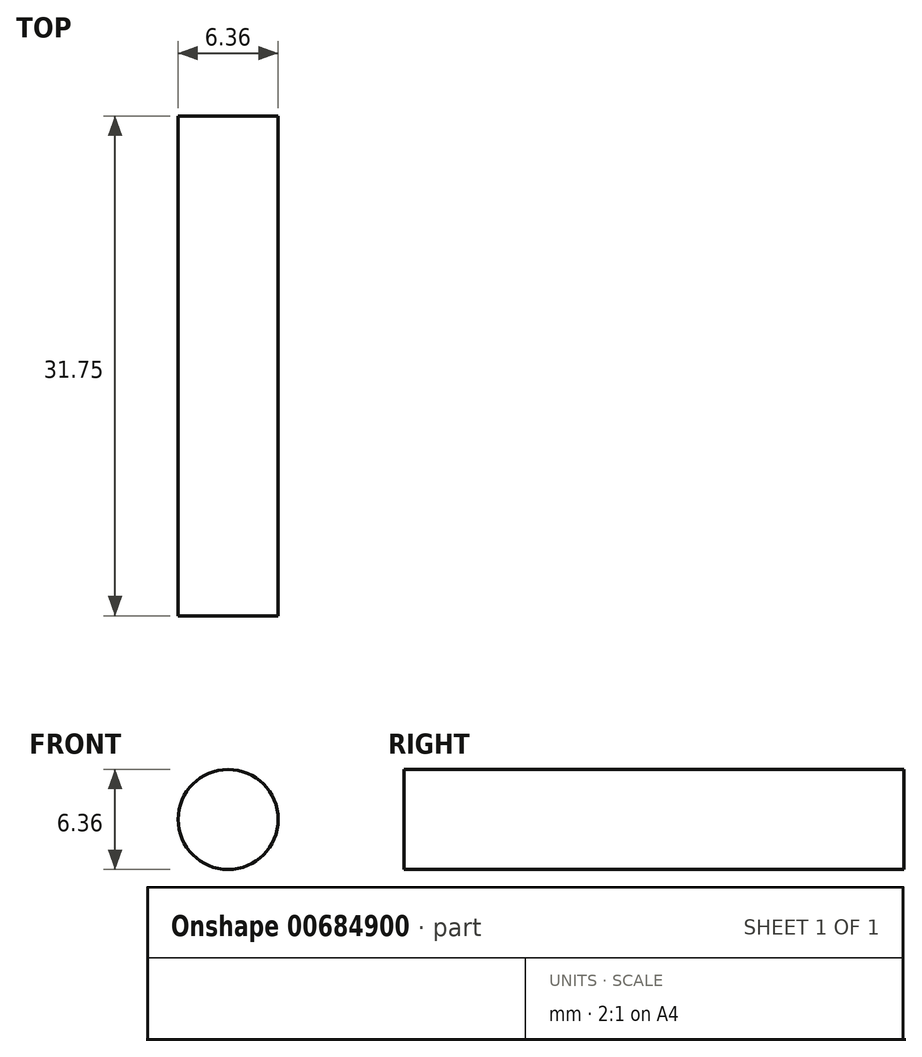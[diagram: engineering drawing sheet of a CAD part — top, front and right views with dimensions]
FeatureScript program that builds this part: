
annotation { "Feature Type Name" : "Feature", "Feature Type Description" : "" }
export const myFeature = defineFeature(function(context is Context, id is Id, definition is map)
    precondition{}
    {
        {
            var Q0;
            Q0=qCreatedBy(makeId("Front.planeOp"),FACE);
            var sketch = newSketch(context, id + "F0", { "sketchPlane" : qUnion([Q0])});
            skCircle(sketch, "E0", {"center": v(0, 0) * mm, "radius": 3.18 * mm});
            skSolve(sketch);
        }
        {
            var Q0;
            Q0 = qSketchRegion(id + "F0", true);
            extrude(context, id + "F1", {"entities" : qUnion([Q0]), "depth" : 31.75 * mm, "offsetDistance" : 25.4 * mm});
        }
    });
